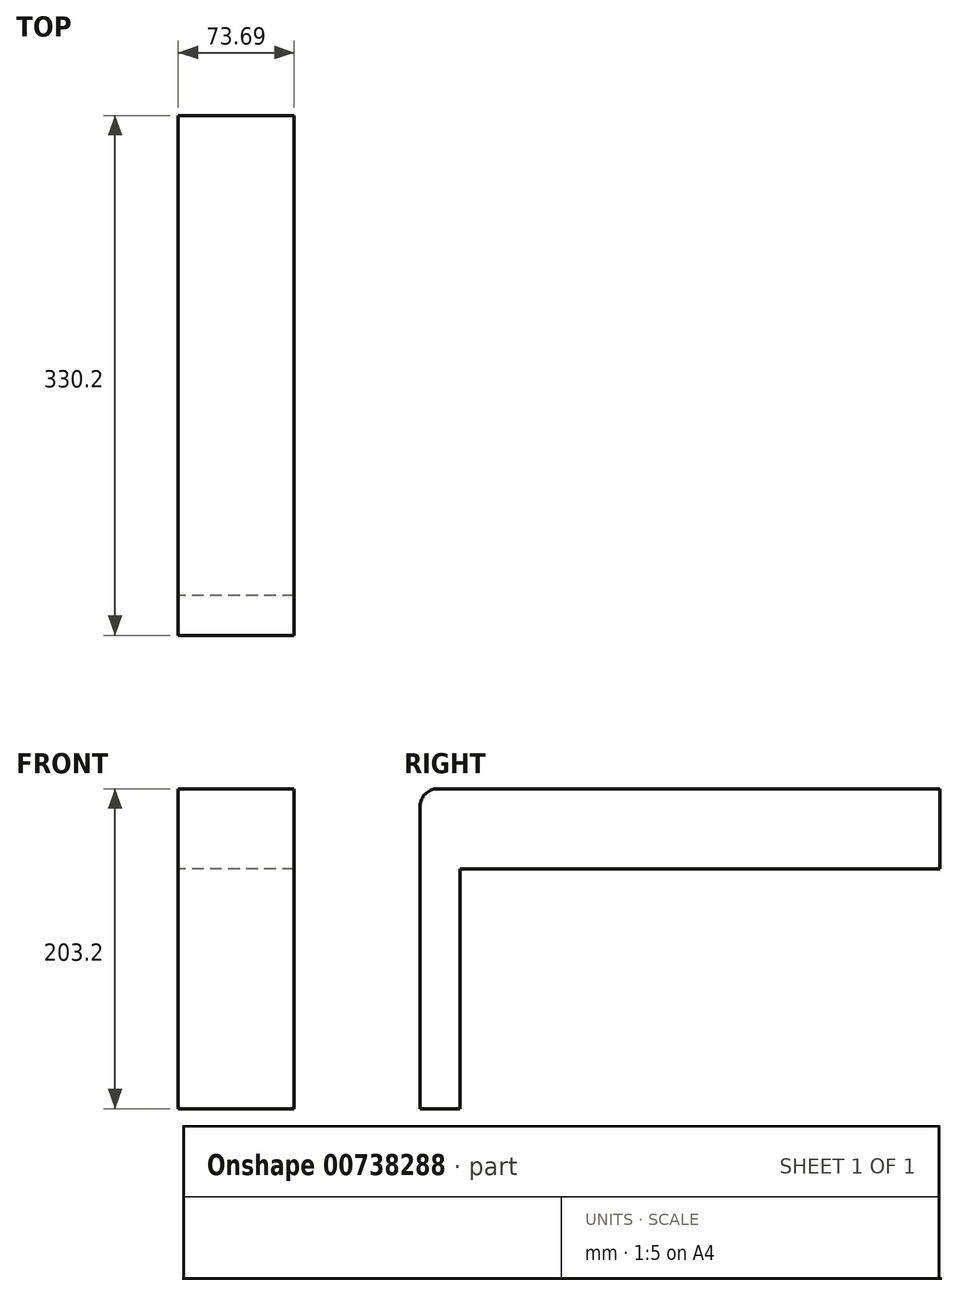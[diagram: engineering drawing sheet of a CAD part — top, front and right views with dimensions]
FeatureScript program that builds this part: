
annotation { "Feature Type Name" : "Feature", "Feature Type Description" : "" }
export const myFeature = defineFeature(function(context is Context, id is Id, definition is map)
    precondition{}
    {
        {
            var Q0;
            Q0=qCreatedBy(makeId("Right.planeOp"),FACE);
            var sketch = newSketch(context, id + "F0", { "sketchPlane" : qUnion([Q0])});
            skLineSegment(sketch, "E0", {"start": v(-304.8, 0) * mm, "end": v(-304.8, 152.4) * mm});
            skLineSegment(sketch, "E1", {"start": v(-304.8, 152.4) * mm, "end": v(0, 152.4) * mm});
            skLineSegment(sketch, "E2", {"start": v(-304.8, 0) * mm, "end": v(-330.2, 0) * mm});
            skLineSegment(sketch, "E3", {"start": v(0, 152.4) * mm, "end": v(0, 203.2) * mm});
            skLineSegment(sketch, "E4", {"start": v(0, 203.2) * mm, "end": v(-319.09, 203.2) * mm});
            skLineSegment(sketch, "E5", {"start": v(-330.2, 192.09) * mm, "end": v(-330.2, 0) * mm});
            skPoint(sketch, "E6.visualSharp", {"position": v(-330.2, 203.2) * mm});
            skArc(sketch, "E6.filletArc", {"start": v(-319.09, 203.2) * mm, "mid": v(-326.95, 199.95) * mm, "end": v(-330.2, 192.09) * mm});
            skSolve(sketch);
        }
        {
            var Q0;
            Q0=makeQuery(id+"F0.imprint","IMPRINT",FACE,{"disambiguationData":[TD([[makeQuery(id+"F0.imprint","IMPRINT",EDGE,{"derivedFrom":sQuery(id+"F0.wireOp",EDGE,"E0")}),1.0]])]});
            extrude(context, id + "F1", {"entities" : qUnion([Q0]), "depth" : (73 + (11 / 16)) * mm, "offsetDistance" : 25.4 * mm});
        }
    });
